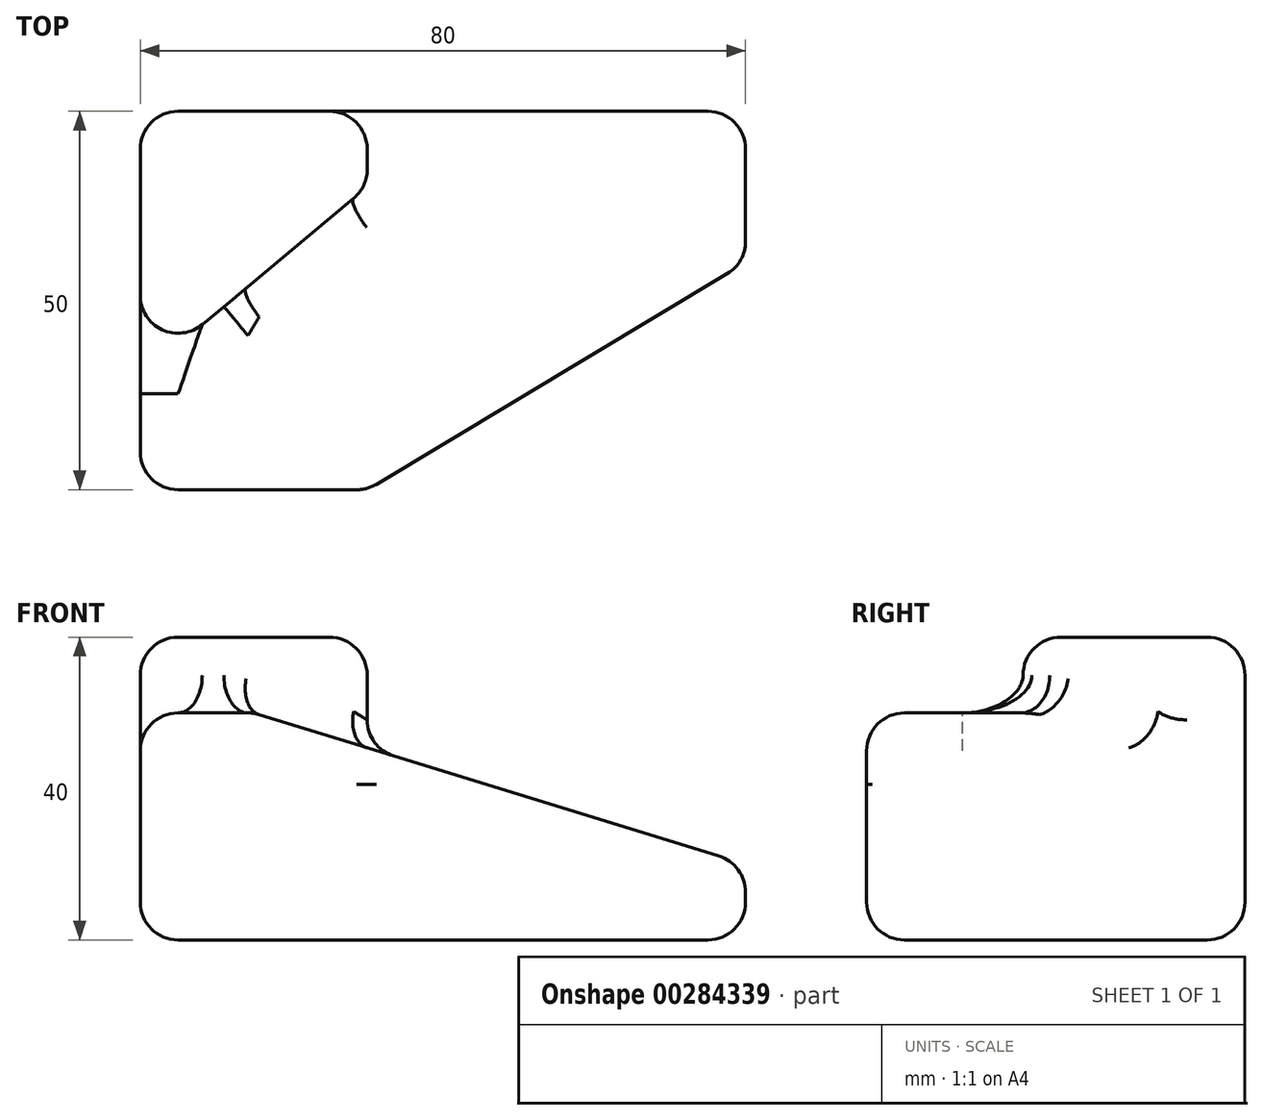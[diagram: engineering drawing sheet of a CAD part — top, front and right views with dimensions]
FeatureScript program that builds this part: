
annotation { "Feature Type Name" : "Feature", "Feature Type Description" : "" }
export const myFeature = defineFeature(function(context is Context, id is Id, definition is map)
    precondition{}
    {
        {
            var Q0;
            Q0=qCreatedBy(makeId("Front.planeOp"),FACE);
            var sketch = newSketch(context, id + "F0", { "sketchPlane" : qUnion([Q0])});
            skLineSegment(sketch, "E0", {"start": v(0, 0) * mm, "end": v(80, 0) * mm});
            skLineSegment(sketch, "E1", {"start": v(80, 0) * mm, "end": v(80, 10) * mm});
            skLineSegment(sketch, "E2", {"start": v(0, 0) * mm, "end": v(0, 30) * mm});
            skLineSegment(sketch, "E3", {"start": v(0, 30) * mm, "end": v(15, 30) * mm});
            skLineSegment(sketch, "E4", {"start": v(15, 30) * mm, "end": v(80, 10) * mm});
            skSolve(sketch);
        }
        {
            var Q0;
            Q0 = qSketchRegion(id + "F0", true);
            extrude(context, id + "F1", {"entities" : qUnion([Q0]), "depth" : 50 * mm});
        }
        {
            var Q0;
            Q0=makeQuery(id+"F1.opExtrude","CAP_EDGE",EDGE,{"disambiguationData":[OSD([sQuery(id+"F0.wireOp",EDGE,"E1")])],"isStart":false});
            chamfer(context, id + "F2", {"entities" : qUnion([Q0]), "chamferType" : ChamferType.TWO_OFFSETS, "width1" : 30 * mm, "oppositeDirection" : true, "width2" : 50 * mm, "tangentPropagation" : true});
        }
        {
            var Q0;
            Q0=qCreatedBy(makeId("Top.planeOp"),FACE);
            var sketch = newSketch(context, id + "F3", { "sketchPlane" : qUnion([Q0])});
            skLineSegment(sketch, "E5", {"start": v(0, 0) * mm, "end": v(30, 0) * mm});
            skLineSegment(sketch, "E6", {"start": v(30, 0) * mm, "end": v(30, -10) * mm});
            skLineSegment(sketch, "E7", {"start": v(0, 0) * mm, "end": v(0, -35) * mm});
            skLineSegment(sketch, "E8", {"start": v(0, -35) * mm, "end": v(30, -10) * mm});
            skSolve(sketch);
        }
        {
            var Q0;
            Q0 = qSketchRegion(id + "F3", true);
            extrude(context, id + "F4", {"entities" : qUnion([Q0]), "operationType" : NewBodyOperationType.ADD, "depth" : 40 * mm});
        }
        {
            var Q0;
            Q0=makeQuery(id+"F4.boolean.opBoolean","INTERSECT",EDGE,{"derivedFrom":[makeQuery(id+"F1.opExtrude","SWEPT_FACE",FACE,{"disambiguationData":[OSD([sQuery(id+"F0.wireOp",EDGE,"E4")])]}),makeQuery(id+"F4.opExtrude","SWEPT_FACE",FACE,{"disambiguationData":[OSD([sQuery(id+"F3.wireOp",EDGE,"E6")])]})]});
            var Q1;
            Q1=makeQuery(id+"F4.opExtrude","CAP_EDGE",EDGE,{"disambiguationData":[OSD([sQuery(id+"F3.wireOp",EDGE,"E8")])],"isStart":false});
            var Q2;
            Q2=makeQuery(id+"F2.opChamfer","BLEND_EDGE",EDGE,{"blendedFrom":[makeQuery(id+"F1.opExtrude","CAP_EDGE",EDGE,{"disambiguationData":[OSD([sQuery(id+"F0.wireOp",EDGE,"E1")])],"isStart":false}),makeQuery(id+"F1.opExtrude","SWEPT_FACE",FACE,{"disambiguationData":[OSD([sQuery(id+"F0.wireOp",EDGE,"E0")])]})],"blendedInto":[makeQuery(id+"F1.opExtrude","SWEPT_FACE",FACE,{"disambiguationData":[OSD([sQuery(id+"F0.wireOp",EDGE,"E0")])]})]});
            var Q3;
            Q3=makeQuery(id+"F2.opChamfer","BLEND_FACE",FACE,{"disambiguationData":[OSD([sQuery(id+"F0.wireOp",EDGE,"E1")])]});
            var Q4;
            Q4=makeQuery(id+"F4.opExtrude","CAP_EDGE",EDGE,{"disambiguationData":[OSD([sQuery(id+"F3.wireOp",EDGE,"E5")])],"isStart":false});
            var Q5;
            Q5=makeQuery(id+"F1.opExtrude","CAP_EDGE",EDGE,{"disambiguationData":[OSD([sQuery(id+"F0.wireOp",EDGE,"E4")])],"isStart":false});
            var Q6;
            Q6=makeQuery(id+"F4.opExtrude","CAP_FACE",FACE,{"disambiguationData":[OSD([sQuery(id+"F3.wireOp",EDGE,"E5"),sQuery(id+"F3.wireOp",EDGE,"E6"),sQuery(id+"F3.wireOp",EDGE,"E7"),sQuery(id+"F3.wireOp",EDGE,"E8")])],"isStart":false});
            var Q7;
            Q7=makeQuery(id+"F4.boolean.opBoolean","MERGE",FACE,{"derivedFrom":[makeQuery(id+"F1.opExtrude","CAP_FACE",FACE,{"disambiguationData":[OSD([sQuery(id+"F0.wireOp",EDGE,"E0"),sQuery(id+"F0.wireOp",EDGE,"E1"),sQuery(id+"F0.wireOp",EDGE,"E2"),sQuery(id+"F0.wireOp",EDGE,"E3"),sQuery(id+"F0.wireOp",EDGE,"E4")])],"isStart":true}),makeQuery(id+"F4.opExtrude","SWEPT_FACE",FACE,{"disambiguationData":[OSD([sQuery(id+"F3.wireOp",EDGE,"E5")])]})]});
            var Q8;
            Q8=makeQuery(id+"F1.opExtrude","CAP_EDGE",EDGE,{"disambiguationData":[OSD([sQuery(id+"F0.wireOp",EDGE,"E2")])],"isStart":false});
            var Q9;
            Q9=makeQuery(id+"F4.boolean.opBoolean","INTERSECT",EDGE,{"derivedFrom":[makeQuery(id+"F1.opExtrude","SWEPT_FACE",FACE,{"disambiguationData":[OSD([sQuery(id+"F0.wireOp",EDGE,"E4")])]}),makeQuery(id+"F4.opExtrude","SWEPT_FACE",FACE,{"disambiguationData":[OSD([sQuery(id+"F3.wireOp",EDGE,"E8")])]})]});
            var Q10;
            Q10=makeQuery(id+"F1.opExtrude","CAP_EDGE",EDGE,{"disambiguationData":[OSD([sQuery(id+"F0.wireOp",EDGE,"E3")])],"isStart":false});
            var Q11;
            Q11=makeQuery(id+"F1.opExtrude","SWEPT_FACE",FACE,{"disambiguationData":[OSD([sQuery(id+"F0.wireOp",EDGE,"E3")])]});
            var Q12;
            Q12=makeQuery(id+"F4.boolean.opBoolean","INTERSECT",EDGE,{"derivedFrom":[makeQuery(id+"F1.opExtrude","SWEPT_FACE",FACE,{"disambiguationData":[OSD([sQuery(id+"F0.wireOp",EDGE,"E3")])]}),makeQuery(id+"F4.opExtrude","SWEPT_FACE",FACE,{"disambiguationData":[OSD([sQuery(id+"F3.wireOp",EDGE,"E8")])]})]});
            var Q13;
            Q13=makeQuery(id+"F4.boolean.opBoolean","MERGE",FACE,{"derivedFrom":[makeQuery(id+"F1.opExtrude","SWEPT_FACE",FACE,{"disambiguationData":[OSD([sQuery(id+"F0.wireOp",EDGE,"E2")])]}),makeQuery(id+"F4.opExtrude","SWEPT_FACE",FACE,{"disambiguationData":[OSD([sQuery(id+"F3.wireOp",EDGE,"E7")])]})]});
            var Q14;
            Q14=makeQuery(id+"F1.opExtrude","CAP_EDGE",EDGE,{"disambiguationData":[OSD([sQuery(id+"F0.wireOp",EDGE,"E0")])],"isStart":false});
            var Q15;
            Q15=makeQuery(id+"F1.opExtrude","SWEPT_FACE",FACE,{"disambiguationData":[OSD([sQuery(id+"F0.wireOp",EDGE,"E0")])]});
            var Q16;
            Q16=makeQuery(id+"F4.opExtrude","SWEPT_FACE",FACE,{"disambiguationData":[OSD([sQuery(id+"F3.wireOp",EDGE,"E6")])]});
            var Q17;
            Q17=makeQuery(id+"F4.opExtrude","SWEPT_FACE",FACE,{"disambiguationData":[OSD([sQuery(id+"F3.wireOp",EDGE,"E8")])]});
            var Q18;
            Q18=makeQuery(id+"F1.opExtrude","SWEPT_FACE",FACE,{"disambiguationData":[OSD([sQuery(id+"F0.wireOp",EDGE,"E4")])]});
            var Q19;
            Q19=makeQuery(id+"F1.opExtrude","CAP_FACE",FACE,{"disambiguationData":[OSD([sQuery(id+"F0.wireOp",EDGE,"E0"),sQuery(id+"F0.wireOp",EDGE,"E1"),sQuery(id+"F0.wireOp",EDGE,"E2"),sQuery(id+"F0.wireOp",EDGE,"E3"),sQuery(id+"F0.wireOp",EDGE,"E4")])],"isStart":false});
            var Q20;
            Q20=makeQuery(id+"F2.opChamfer","BLEND_EDGE",EDGE,{"blendedFrom":[makeQuery(id+"F1.opExtrude","CAP_EDGE",EDGE,{"disambiguationData":[OSD([sQuery(id+"F0.wireOp",EDGE,"E1")])],"isStart":false}),makeQuery(id+"F1.opExtrude","SWEPT_FACE",FACE,{"disambiguationData":[OSD([sQuery(id+"F0.wireOp",EDGE,"E4")])]})],"blendedInto":[makeQuery(id+"F1.opExtrude","SWEPT_FACE",FACE,{"disambiguationData":[OSD([sQuery(id+"F0.wireOp",EDGE,"E4")])]})]});
            var Q21;
            {var subQ0=sQuery(id+"F0.wireOp",EDGE,"E1");Q21=makeQuery(id+"F2.opChamfer","BLEND_EDGE",EDGE,{"blendedFrom":[makeQuery(id+"F1.opExtrude","CAP_EDGE",EDGE,{"disambiguationData":[OSD([subQ0])],"isStart":false}),makeQuery(id+"F1.opExtrude","SWEPT_FACE",FACE,{"disambiguationData":[OSD([subQ0])]})],"blendedInto":[makeQuery(id+"F1.opExtrude","SWEPT_FACE",FACE,{"disambiguationData":[OSD([subQ0])]})]});}
            var Q22;
            Q22=makeQuery(id+"F1.opExtrude","SWEPT_FACE",FACE,{"disambiguationData":[OSD([sQuery(id+"F0.wireOp",EDGE,"E1")])]});
            var Q23;
            Q23=makeQuery(id+"F4.opExtrude","CAP_EDGE",EDGE,{"disambiguationData":[OSD([sQuery(id+"F3.wireOp",EDGE,"E7")])],"isStart":false});
            var Q24;
            Q24=makeQuery(id+"F1.opExtrude","SWEPT_EDGE",EDGE,{"disambiguationData":[OSD([sQuery(id+"F0.wireOp",EDGE,"E1"),sQuery(id+"F0.wireOp",EDGE,"E4")])]});
            var Q25;
            Q25=makeQuery(id+"F1.opExtrude","SWEPT_EDGE",EDGE,{"disambiguationData":[OSD([sQuery(id+"F0.wireOp",EDGE,"E0"),sQuery(id+"F0.wireOp",EDGE,"E1")])]});
            var Q26;
            Q26=makeQuery(id+"F4.opExtrude","CAP_EDGE",EDGE,{"disambiguationData":[OSD([sQuery(id+"F3.wireOp",EDGE,"E6")])],"isStart":false});
            var Q27;
            Q27=makeQuery(id+"F4.boolean.opBoolean","MERGE",EDGE,{"derivedFrom":[makeQuery(id+"F1.opExtrude","CAP_EDGE",EDGE,{"disambiguationData":[OSD([sQuery(id+"F0.wireOp",EDGE,"E2")])],"isStart":true}),makeQuery(id+"F4.opExtrude","SWEPT_EDGE",EDGE,{"disambiguationData":[OSD([sQuery(id+"F3.wireOp",EDGE,"E5"),sQuery(id+"F3.wireOp",EDGE,"E7")])]})]});
            var Q28;
            Q28=makeQuery(id+"F1.opExtrude","SWEPT_EDGE",EDGE,{"disambiguationData":[OSD([sQuery(id+"F0.wireOp",EDGE,"E0"),sQuery(id+"F0.wireOp",EDGE,"E2")])]});
            var Q29;
            {var subQ0=sQuery(id+"F0.wireOp",EDGE,"E1");Q29=makeQuery(id+"F2.opChamfer","BLEND_EDGE",EDGE,{"blendedFrom":[makeQuery(id+"F1.opExtrude","CAP_EDGE",EDGE,{"disambiguationData":[OSD([subQ0])],"isStart":false}),makeQuery(id+"F1.opExtrude","CAP_FACE",FACE,{"disambiguationData":[OSD([sQuery(id+"F0.wireOp",EDGE,"E0"),subQ0,sQuery(id+"F0.wireOp",EDGE,"E2"),sQuery(id+"F0.wireOp",EDGE,"E3"),sQuery(id+"F0.wireOp",EDGE,"E4")])],"isStart":false})],"blendedInto":[makeQuery(id+"F1.opExtrude","CAP_FACE",FACE,{"disambiguationData":[OSD([sQuery(id+"F0.wireOp",EDGE,"E0"),subQ0,sQuery(id+"F0.wireOp",EDGE,"E2"),sQuery(id+"F0.wireOp",EDGE,"E3"),sQuery(id+"F0.wireOp",EDGE,"E4")])],"isStart":false})]});}
            var Q30;
            Q30=makeQuery(id+"F1.opExtrude","SWEPT_EDGE",EDGE,{"disambiguationData":[OSD([sQuery(id+"F0.wireOp",EDGE,"E2"),sQuery(id+"F0.wireOp",EDGE,"E3")])]});
            var Q31;
            Q31=makeQuery(id+"F4.opExtrude","SWEPT_EDGE",EDGE,{"disambiguationData":[OSD([sQuery(id+"F3.wireOp",EDGE,"E7"),sQuery(id+"F3.wireOp",EDGE,"E8")])]});
            var Q32;
            Q32=makeQuery(id+"F1.opExtrude","CAP_EDGE",EDGE,{"disambiguationData":[OSD([sQuery(id+"F0.wireOp",EDGE,"E0")])],"isStart":true});
            var Q33;
            Q33=makeQuery(id+"F4.opExtrude","SWEPT_EDGE",EDGE,{"disambiguationData":[OSD([sQuery(id+"F3.wireOp",EDGE,"E6"),sQuery(id+"F3.wireOp",EDGE,"E8")])]});
            var Q34;
            Q34=makeQuery(id+"F1.opExtrude","SWEPT_EDGE",EDGE,{"disambiguationData":[OSD([sQuery(id+"F0.wireOp",EDGE,"E3"),sQuery(id+"F0.wireOp",EDGE,"E4")])]});
            var Q35;
            Q35=makeQuery(id+"F4.opExtrude","SWEPT_EDGE",EDGE,{"disambiguationData":[OSD([sQuery(id+"F3.wireOp",EDGE,"E5"),sQuery(id+"F3.wireOp",EDGE,"E6")])]});
            var Q36;
            Q36=makeQuery(id+"F1.opExtrude","CAP_EDGE",EDGE,{"disambiguationData":[OSD([sQuery(id+"F0.wireOp",EDGE,"E4")])],"isStart":true});
            var Q37;
            Q37=makeQuery(id+"F1.opExtrude","CAP_EDGE",EDGE,{"disambiguationData":[OSD([sQuery(id+"F0.wireOp",EDGE,"E1")])],"isStart":true});
            fillet(context, id + "F5", {"entities" : qUnion([Q0, Q1, Q2, Q3, Q4, Q5, Q6, Q7, Q8, Q9, Q10, Q11, Q12, Q13, Q14, Q15, Q16, Q17, Q18, Q19, Q20, Q21, Q22, Q23, Q24, Q25, Q26, Q27, Q28, Q29, Q30, Q31, Q32, Q33, Q34, Q35, Q36, Q37]), "radius" : 5 * mm, "tangentPropagation" : true, "allowEdgeOverflow" : false});
        }
    });
